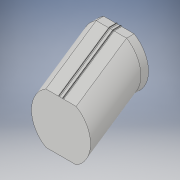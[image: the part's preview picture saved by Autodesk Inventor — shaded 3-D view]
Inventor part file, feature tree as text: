
AUTODESK INVENTOR PART (.ipt)
format: ipt  version: 2017 (Build 210142000, 142)  size: 156,160 bytes
history: native  units: in
note: dims shown in document units (in); Inventor stores cm internally (conversion verified against a paired STEP export)
features: sketch x2, extrude x1, plane x1, sweep x1
ambient origin geometry x8: Origin, YZ Plane, XZ Plane, XY Plane, X Axis, Y Axis, Z Axis, Center Point
bodies: Solid1 (feature_tree)
feature tree (5):
  sketch  "Sketch1"  dims[d0=6.6667in d3=1.0in d4=0.0in d12=8.0in]
  extrude  "connecction top"  Depth=6.6667in
  plane  "Work Plane2"
  sweep  "ramp"
  sketch  "Sketch6"  dims[d28=8.0in d45=0.0in d46=0.0in d49=4.0in d50=0.5833in d51=3.8873in d52=3.8873in d53=1.7083in d54=0.0625in d55=0.0625in d56=1.6458in d57=0.125in d58=0.25in d59=0.125in d60=0.0892in d61=0.0884in d62=45.0deg d63=3.3333in d64=0.125in d65=0.8521in]
